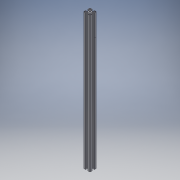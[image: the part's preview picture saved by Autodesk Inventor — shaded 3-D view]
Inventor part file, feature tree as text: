
AUTODESK INVENTOR PART (.ipt)
format: ipt  version: 2019 (Build 230136000, 136)  size: 342,528 bytes
history: native  units: in
note: dims shown in document units (in); Inventor stores cm internally (conversion verified against a paired STEP export)
features: extrude x1, sketch x1, projected_geometry x1
ambient origin geometry x8: Origin, YZ Plane, XZ Plane, XY Plane, X Axis, Y Axis, Z Axis, Center Point
bodies: Solid1 (feature_tree), Body1 (feature_tree)
feature tree (3):
  extrude  "Extrusion1"  [1 undecoded]
  sketch  "Sketch1"  dims[d0=20.8661in d1=0.0in]
  projected_geometry  "Projected Loop1"
note: 1 required parameter value undecoded (feature->parameter linkage not recoverable at this tier; creation-order binding heuristic only, values carry confidence <= 0.55)
